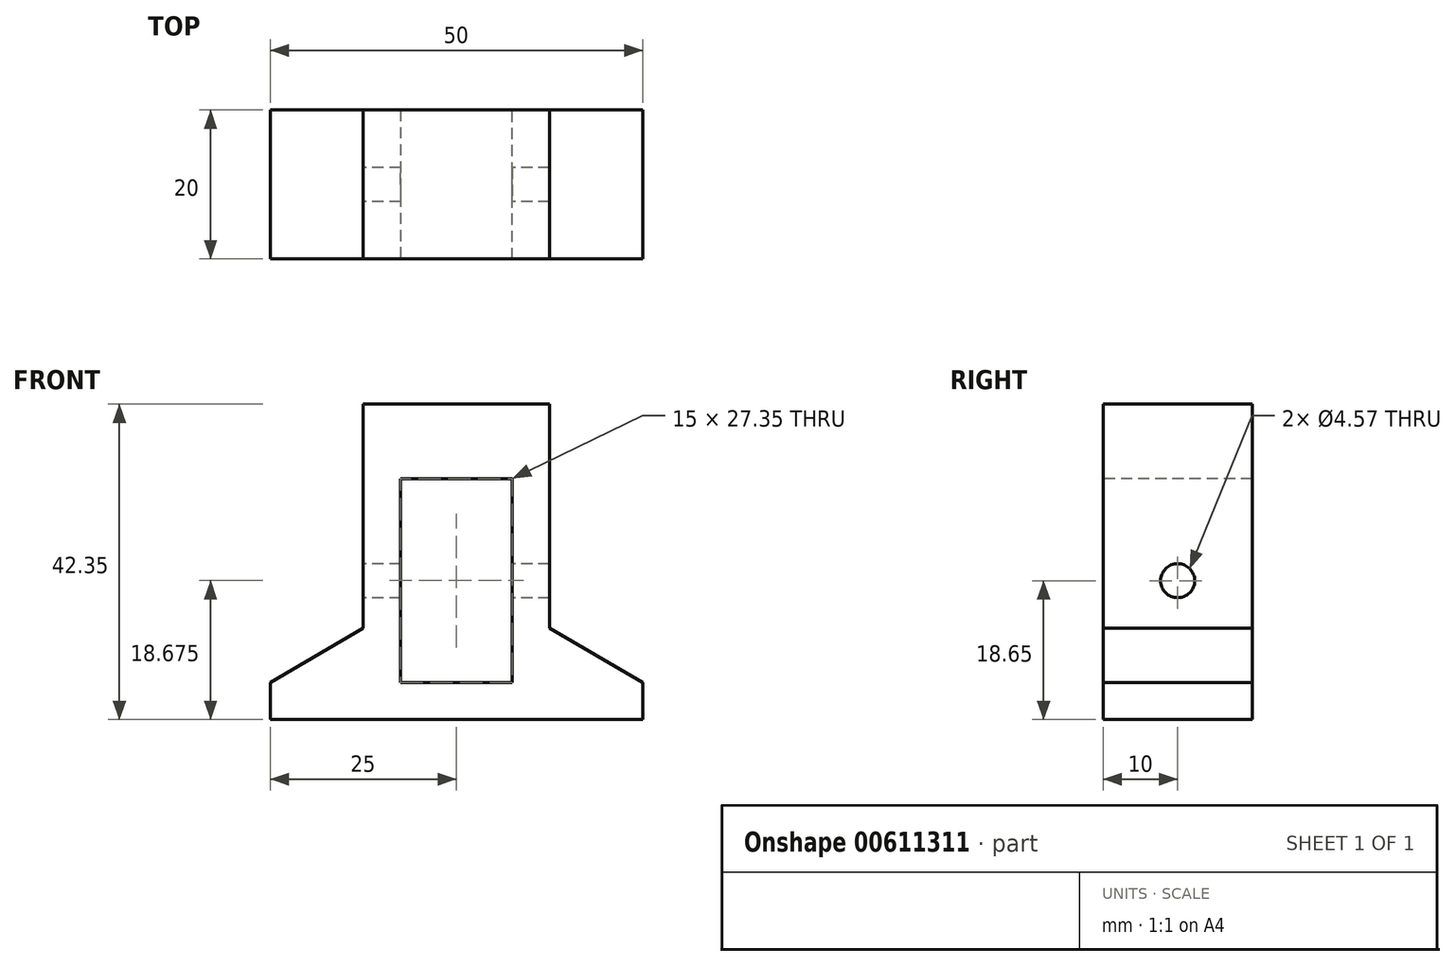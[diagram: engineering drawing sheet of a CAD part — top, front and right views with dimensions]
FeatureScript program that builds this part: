
annotation { "Feature Type Name" : "Feature", "Feature Type Description" : "" }
export const myFeature = defineFeature(function(context is Context, id is Id, definition is map)
    precondition{}
    {
        {
            var Q0;
            Q0=qCreatedBy(makeId("Top.planeOp"),FACE);
            var sketch = newSketch(context, id + "F0", { "sketchPlane" : qUnion([Q0])});
            skLineSegment(sketch, "E0.bottom", {"start": v(25, 10) * mm, "end": v(-25, 10) * mm});
            skLineSegment(sketch, "E0.top", {"start": v(25, -10) * mm, "end": v(-25, -10) * mm});
            skLineSegment(sketch, "E0.left", {"start": v(25, 10) * mm, "end": v(25, -10) * mm});
            skLineSegment(sketch, "E0.right", {"start": v(-25, 10) * mm, "end": v(-25, -10) * mm});
            skPoint(sketch, "E0.middle", {"position": v(0, 0) * mm});
            skSolve(sketch);
        }
        {
            var Q0;
            Q0=makeQuery(id+"F0.imprint","IMPRINT",FACE,{"disambiguationData":[TD([[makeQuery(id+"F0.imprint","IMPRINT",EDGE,{"derivedFrom":sQuery(id+"F0.wireOp",EDGE,"E0.bottom")}),1.0]])]});
            extrude(context, id + "F1", {"entities" : qUnion([Q0]), "depth" : 5 * mm, "offsetDistance" : 25 * mm});
        }
        {
            var Q0;
            Q0=makeQuery(id+"F1.opExtrude","CAP_FACE",FACE,{"disambiguationData":[OSD([sQuery(id+"F0.wireOp",EDGE,"E0.bottom"),sQuery(id+"F0.wireOp",EDGE,"E0.top"),sQuery(id+"F0.wireOp",EDGE,"E0.left"),sQuery(id+"F0.wireOp",EDGE,"E0.right")])],"isStart":false});
            var sketch = newSketch(context, id + "F2", { "sketchPlane" : qUnion([Q0])});
            skLineSegment(sketch, "E1.bottom", {"start": v(25, -10) * mm, "end": v(7.5, -10) * mm});
            skLineSegment(sketch, "E1.top", {"start": v(25, 10) * mm, "end": v(7.5, 10) * mm});
            skLineSegment(sketch, "E1.left", {"start": v(25, -10) * mm, "end": v(25, 10) * mm});
            skLineSegment(sketch, "E1.right", {"start": v(7.5, -10) * mm, "end": v(7.5, 10) * mm});
            skLineSegment(sketch, "E2.bottom", {"start": v(-25, 10) * mm, "end": v(-7.5, 10) * mm});
            skLineSegment(sketch, "E2.top", {"start": v(-25, -10) * mm, "end": v(-7.5, -10) * mm});
            skLineSegment(sketch, "E2.left", {"start": v(-25, 10) * mm, "end": v(-25, -10) * mm});
            skLineSegment(sketch, "E2.right", {"start": v(-7.5, 10) * mm, "end": v(-7.5, -10) * mm});
            skSolve(sketch);
        }
        {
            var Q0;
            Q0 = qSketchRegion(id + "F2", true);
            extrude(context, id + "F3", {"entities" : qUnion([Q0]), "operationType" : NewBodyOperationType.ADD, "depth" : 20 * mm, "offsetDistance" : 25 * mm});
        }
        {
            var Q0;
            Q0=makeQuery(id+"F3.boolean.opBoolean","MERGE",FACE,{"derivedFrom":[makeQuery(id+"F1.opExtrude","SWEPT_FACE",FACE,{"disambiguationData":[OSD([sQuery(id+"F0.wireOp",EDGE,"E0.bottom")])]}),makeQuery(id+"F3.opExtrude","SWEPT_FACE",FACE,{"disambiguationData":[OSD([sQuery(id+"F2.wireOp",EDGE,"E1.top")])]}),makeQuery(id+"F3.opExtrude","SWEPT_FACE",FACE,{"disambiguationData":[OSD([sQuery(id+"F2.wireOp",EDGE,"E2.bottom")])]})]});
            var sketch = newSketch(context, id + "F4", { "sketchPlane" : qUnion([Q0])});
            skPoint(sketch, "E3", {"position": v(-7.5, 12.3) * mm});
            skPoint(sketch, "E4", {"position": v(7.5, 12.3) * mm});
            skLineSegment(sketch, "E5", {"start": v(7.5, 12.3) * mm, "end": v(7.5, 25) * mm});
            skLineSegment(sketch, "E6", {"start": v(12.5, 12.3) * mm, "end": v(7.5, 12.3) * mm});
            skLineSegment(sketch, "E7", {"start": v(-7.5, 12.3) * mm, "end": v(-7.5, 25) * mm});
            skLineSegment(sketch, "E8", {"start": v(-12.5, 12.3) * mm, "end": v(-7.5, 12.3) * mm});
            skLineSegment(sketch, "E9", {"start": v(-12.5, 12.3) * mm, "end": v(-25, 5) * mm});
            skLineSegment(sketch, "E10", {"start": v(12.5, 12.3) * mm, "end": v(25, 5) * mm});
            skLineSegment(sketch, "E11", {"start": v(-12.5, 12.3) * mm, "end": v(-12.5, 25) * mm});
            skLineSegment(sketch, "E12", {"start": v(-12.5, 25) * mm, "end": v(-7.5, 25) * mm});
            skLineSegment(sketch, "E13", {"start": v(7.5, 25) * mm, "end": v(12.5, 25) * mm});
            skLineSegment(sketch, "E14", {"start": v(12.5, 25) * mm, "end": v(12.5, 12.3) * mm});
            skSolve(sketch);
        }
        {
            var Q0;
            {var subQ0=sQuery(id+"F4.wireOp",EDGE,"E9");Q0=makeQuery(id+"F4.imprint","IMPRINT",FACE,{"disambiguationData":[TD([[makeQuery(id+"F4.imprint","IMPRINT",EDGE,{"derivedFrom":subQ0}),-1.0]])]});}
            var Q1;
            {var subQ0=sQuery(id+"F4.wireOp",EDGE,"E10");Q1=makeQuery(id+"F4.imprint","IMPRINT",FACE,{"disambiguationData":[TD([[makeQuery(id+"F4.imprint","IMPRINT",EDGE,{"derivedFrom":subQ0}),1.0]])]});}
            extrude(context, id + "F5", {"entities" : qUnion([Q0, Q1]), "operationType" : NewBodyOperationType.REMOVE, "endBound" : BoundingType.THROUGH_ALL, "oppositeDirection" : true, "depth" : 25 * mm, "offsetDistance" : 25 * mm});
        }
        {
            var Q0;
            Q0=makeQuery(id+"F5.boolean.opBoolean","COPY",FACE,{"derivedFrom":makeQuery(id+"F5.opExtrude","SWEPT_FACE",FACE,{"disambiguationData":[OSD([sQuery(id+"F4.wireOp",EDGE,"E14")])]})});
            var sketch = newSketch(context, id + "F6", { "sketchPlane" : qUnion([Q0])});
            skLineSegment(sketch, "E15", {"start": v(-10, 25) * mm, "end": v(10, 12.3) * mm, "construction": true});
            skLineSegment(sketch, "E16", {"start": v(10, 25) * mm, "end": v(-10, 12.3) * mm, "construction": true});
            skCircle(sketch, "E17", {"center": v(0, 18.65) * mm, "radius": 2.29 * mm});
            skSolve(sketch);
        }
        {
            var Q0;
            Q0=makeQuery(id+"F6.imprint","IMPRINT",FACE,{"disambiguationData":[TD([[makeQuery(id+"F6.imprint","IMPRINT",EDGE,{"derivedFrom":sQuery(id+"F6.wireOp",EDGE,"E17")}),1.0]])]});
            extrude(context, id + "F7", {"entities" : qUnion([Q0]), "operationType" : NewBodyOperationType.REMOVE, "endBound" : BoundingType.THROUGH_ALL, "oppositeDirection" : true, "depth" : 25 * mm, "offsetDistance" : 25 * mm});
        }
        {
            var Q0;
            Q0=makeQuery(id+"F3.opExtrude","CAP_FACE",FACE,{"disambiguationData":[OSD([sQuery(id+"F2.wireOp",EDGE,"E2.bottom"),sQuery(id+"F2.wireOp",EDGE,"E2.top"),sQuery(id+"F2.wireOp",EDGE,"E2.left"),sQuery(id+"F2.wireOp",EDGE,"E2.right")])],"isStart":false});
            var Q1;
            Q1=makeQuery(id+"F3.opExtrude","CAP_FACE",FACE,{"disambiguationData":[OSD([sQuery(id+"F2.wireOp",EDGE,"E1.bottom"),sQuery(id+"F2.wireOp",EDGE,"E1.top"),sQuery(id+"F2.wireOp",EDGE,"E1.left"),sQuery(id+"F2.wireOp",EDGE,"E1.right")])],"isStart":false});
            extrude(context, id + "F8", {"entities" : qUnion([Q0, Q1]), "operationType" : NewBodyOperationType.ADD, "depth" : 17.35 * mm, "offsetDistance" : 25 * mm});
        }
        {
            var Q0;
            {var subQ0=sQuery(id+"F4.wireOp",EDGE,"E11");Q0=makeQuery(id+"F8.boolean.opBoolean","MERGE",FACE,{"derivedFrom":[makeQuery(id+"F5.boolean.opBoolean","COPY",FACE,{"derivedFrom":makeQuery(id+"F5.opExtrude","SWEPT_FACE",FACE,{"disambiguationData":[OSD([subQ0])]})}),makeQuery(id+"F8.opExtrude","SWEPT_FACE",FACE,{"disambiguationData":[OSD([sQuery(id+"F2.wireOp",EDGE,"E1.top"),subQ0,sQuery(id+"F4.wireOp",EDGE,"E12")])]})]});}
            var sketch = newSketch(context, id + "F9", { "sketchPlane" : qUnion([Q0])});
            skLineSegment(sketch, "E18", {"start": v(-10, 32.35) * mm, "end": v(10, 32.35) * mm});
            skSolve(sketch);
        }
        {
            var Q0;
            Q0 = qSketchRegion(id + "F9", true);
            var Q1;
            {var subQ0=sQuery(id+"F9.wireOp",EDGE,"E18");Q1=makeQuery(id+"F9.imprint","IMPRINT",FACE,{"disambiguationData":[TD([[makeQuery(id+"F9.imprint","IMPRINT",EDGE,{"derivedFrom":subQ0}),1.0]])]});}
            var Q2;
            {var subQ0=sQuery(id+"F4.wireOp",EDGE,"E14");Q2=makeQuery(id+"F8.boolean.opBoolean","MERGE",FACE,{"derivedFrom":[makeQuery(id+"F5.boolean.opBoolean","COPY",FACE,{"derivedFrom":makeQuery(id+"F5.opExtrude","SWEPT_FACE",FACE,{"disambiguationData":[OSD([subQ0])]})}),makeQuery(id+"F8.opExtrude","SWEPT_FACE",FACE,{"disambiguationData":[OSD([sQuery(id+"F2.wireOp",EDGE,"E2.bottom"),sQuery(id+"F4.wireOp",EDGE,"E13"),subQ0])]})]});}
            extrude(context, id + "F10", {"entities" : qUnion([Q0, Q1]), "operationType" : NewBodyOperationType.ADD, "endBound" : BoundingType.UP_TO_SURFACE, "oppositeDirection" : true, "depth" : 25 * mm, "endBoundEntityFace" : qUnion([Q2]), "offsetDistance" : 25 * mm});
        }
    });
